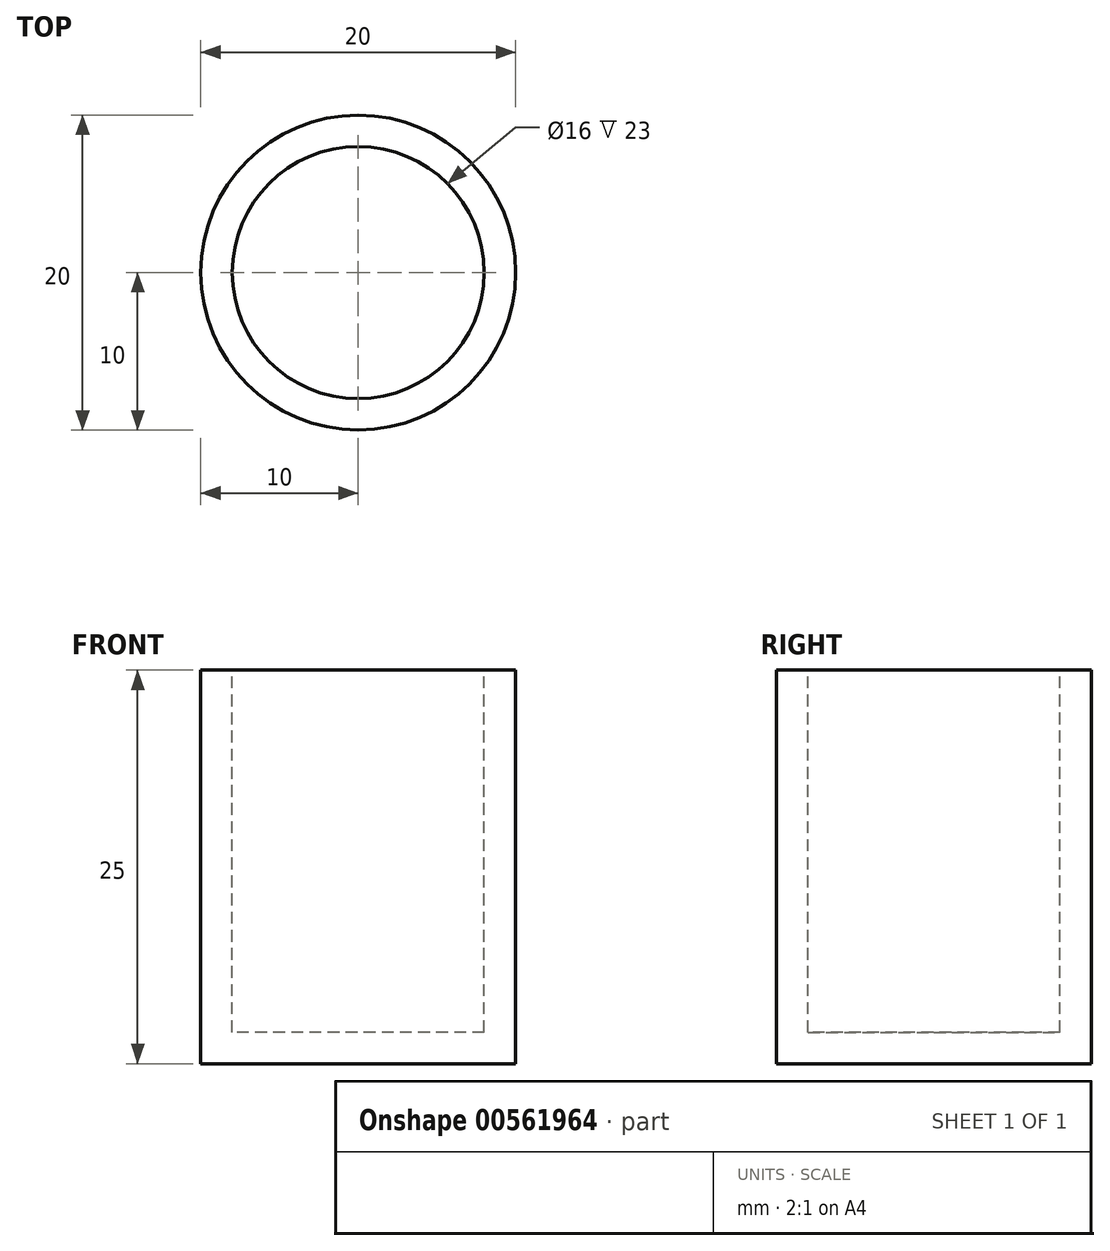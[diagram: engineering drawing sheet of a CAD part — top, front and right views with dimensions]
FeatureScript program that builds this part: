
annotation { "Feature Type Name" : "Feature", "Feature Type Description" : "" }
export const myFeature = defineFeature(function(context is Context, id is Id, definition is map)
    precondition{}
    {
        {
            var Q0;
            Q0=qCreatedBy(makeId("Front.planeOp"),FACE);
            var sketch = newSketch(context, id + "F0", { "sketchPlane" : qUnion([Q0])});
            skLineSegment(sketch, "E0", {"start": v(0, 0) * mm, "end": v(10, 0) * mm});
            skLineSegment(sketch, "E1", {"start": v(10, 0) * mm, "end": v(10, 25) * mm});
            skLineSegment(sketch, "E2", {"start": v(10, 25) * mm, "end": v(8, 25) * mm});
            skLineSegment(sketch, "E3", {"start": v(8, 25) * mm, "end": v(8, 2) * mm});
            skLineSegment(sketch, "E4", {"start": v(8, 2) * mm, "end": v(0, 2) * mm});
            skLineSegment(sketch, "E5", {"start": v(0, 2) * mm, "end": v(0, 0) * mm});
            skSolve(sketch);
        }
        {
            var Q0;
            Q0=makeQuery(id+"F0.imprint","IMPRINT",FACE,{"disambiguationData":[TD([[makeQuery(id+"F0.imprint","IMPRINT",EDGE,{"derivedFrom":sQuery(id+"F0.wireOp",EDGE,"E0")}),1.0]])]});
            var Q1;
            Q1=sQuery(id+"F0.wireOp",EDGE,"E5");
            revolve(context, id + "F1", {"entities" : qUnion([Q0]), "axis" : qUnion([Q1]), "revolveType" : RevolveType.FULL});
        }
    });
